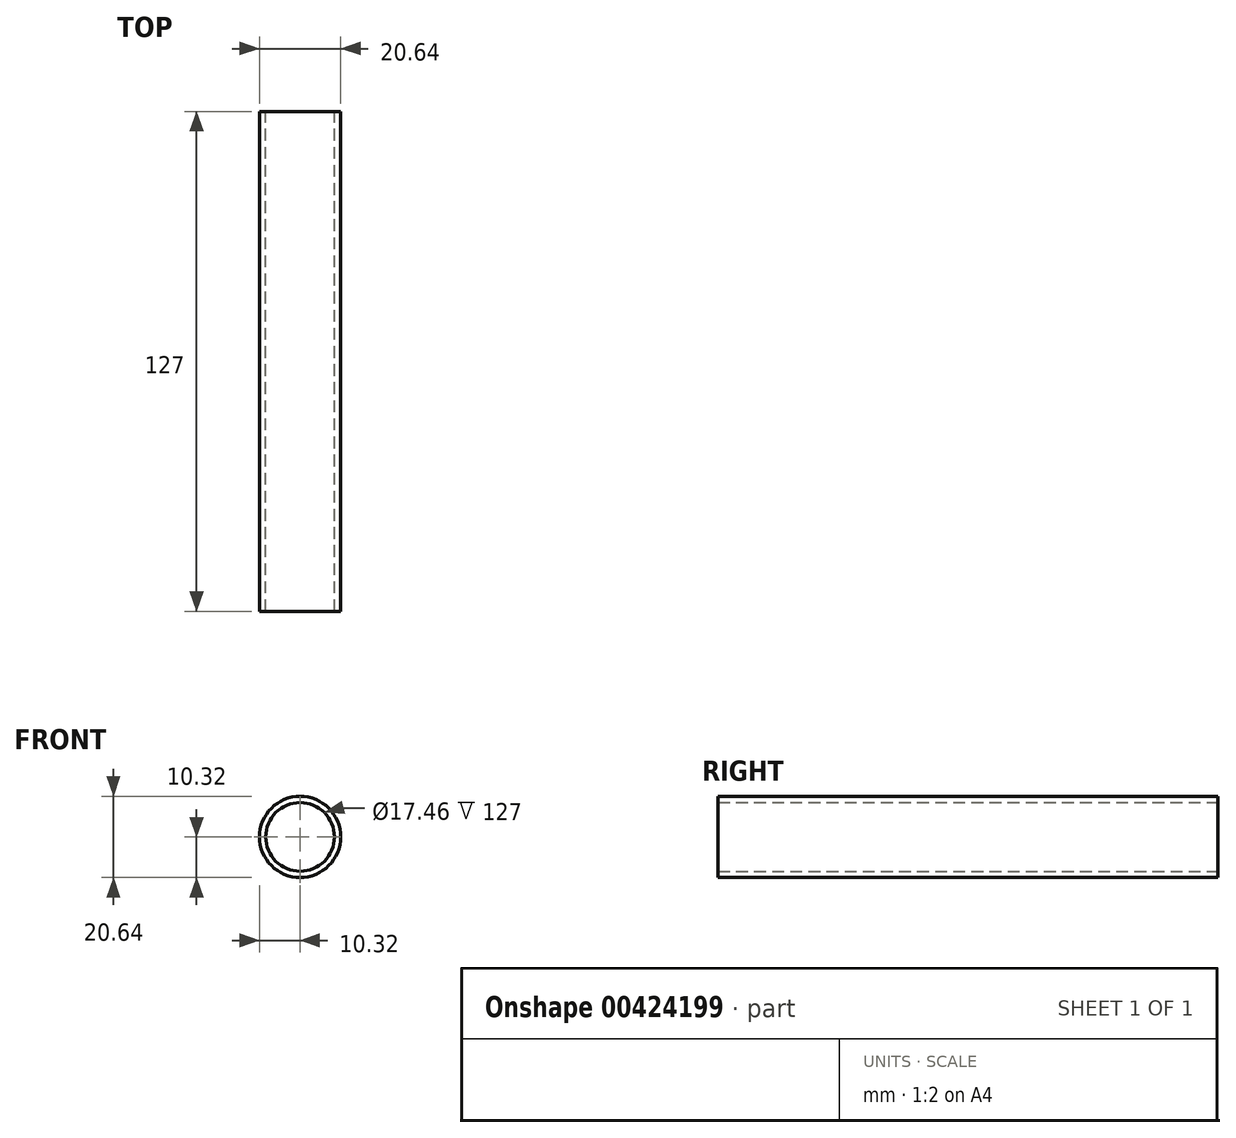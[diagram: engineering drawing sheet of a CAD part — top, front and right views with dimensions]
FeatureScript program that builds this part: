
annotation { "Feature Type Name" : "Feature", "Feature Type Description" : "" }
export const myFeature = defineFeature(function(context is Context, id is Id, definition is map)
    precondition{}
    {
        {
            var Q0;
            Q0=qCreatedBy(makeId("Front.planeOp"),FACE);
            var sketch = newSketch(context, id + "F0", { "sketchPlane" : qUnion([Q0])});
            skCircle(sketch, "E0", {"center": v(0, 0) * mm, "radius": 10.32 * mm});
            skCircle(sketch, "E1", {"center": v(0, 0) * mm, "radius": 8.73 * mm});
            skSolve(sketch);
        }
        {
            var Q0;
            Q0=makeQuery(id+"F0.imprint","IMPRINT",FACE,{"disambiguationData":[TD([[makeQuery(id+"F0.imprint","IMPRINT",EDGE,{"derivedFrom":sQuery(id+"F0.wireOp",EDGE,"E0")}),1.0]])]});
            extrude(context, id + "F1", {"entities" : qUnion([Q0]), "depth" : 127 * mm});
        }
    });
